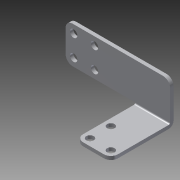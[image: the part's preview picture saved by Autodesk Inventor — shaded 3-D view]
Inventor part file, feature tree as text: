
AUTODESK INVENTOR PART (.ipt)
format: ipt  version: 2014 SP1 (Build 180222100, 222)  size: 152,576 bytes
history: native  units: in
note: dims shown in document units (in); Inventor stores cm internally (conversion verified against a paired STEP export)
features: sheet_metal_op x2, sketch x1, other x1
ambient origin geometry x8: Origin, YZ Plane, XZ Plane, XY Plane, X Axis, Y Axis, Z Axis, Center Point
bodies: Solid1 (feature_tree)
feature tree (4):
  sketch  "Sketch1"  dims[d0=0.25in d1=1.325in d2=1.25in d3=0.75in d4=0.75in d5=0.75in d6=0.75in d7=0.266in d8=0.266in d9=1.4075in d10=3.75in d11=3.5649in d12=0.2875in d13=0.2875in d14=0.25in d15=0.25in d16=0.75in d17=0.125in d18=0.125in d19=0.0625in d20=0.25in d21=0.125in d22=90.0deg d23=0.05in]
  sheet_metal_op  "Face1"
  sheet_metal_op  "Fold1"
  other  "Plate1"
